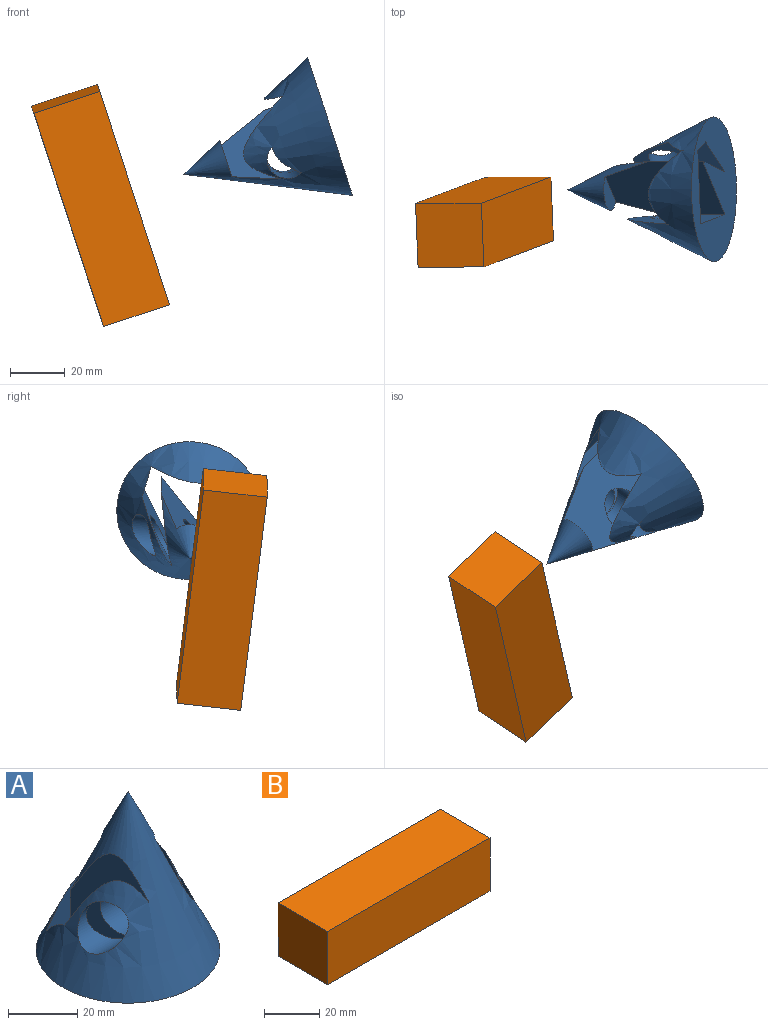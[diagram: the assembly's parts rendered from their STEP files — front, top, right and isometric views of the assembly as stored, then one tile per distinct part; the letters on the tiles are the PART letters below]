
ASSEMBLY  parts=2 mates=1
PART A: 12 faces, bbox 55.3x55.3x58.5 mm
  f0: plane 53.16x53.16mm, normal (0,0,-1), area 1696.5mm2, adj f2,f6,f7,f8,f9,f10,f11
  f1: cylinder r=7.21mm len=25.05mm, axis (-1,0,0), area 694mm2, adj f2,f4,f8,f9,f10
  f2: cone r=26.58mm half-angle=25.2deg, axis (0,0,-1), area 3909.5mm2, adj f0,f1,f3,f4,f5,f6,f7,f8
  f3: cylinder r=7.21mm len=15.14mm, axis (-1,0,0), area 265.4mm2, adj f2,f11
  f4: plane 13.37x10.95mm, normal (-1,0,0), area 98.6mm2, adj f1,f2
  f5: plane 13.47x13.25mm, normal (0,0,-1), area 97.6mm2, adj f2,f9
  f6: plane 26.97x19.73mm, normal (0,-1,0), area 429.8mm2, adj f0,f2,f7,f8
  f7: plane 16.27x11.73mm, normal (0.97,-0.22,0), area 106.1mm2, adj f0,f2,f6,f11
  f8: plane 33.5x28.91mm, normal (-1,0,0), area 630.2mm2, adj f0,f1,f2,f6,f9
  f9: plane 41.38x24.9mm, normal (0.72,0.69,0), area 923.7mm2, adj f0,f1,f2,f5,f8,f10
  f10: plane 39.04x25.37mm, normal (-0.96,-0.26,0), area 693.9mm2, adj f0,f1,f2,f9,f11
  f11: plane 34.14x22.86mm, normal (0.84,0.54,0), area 485.6mm2, adj f0,f2,f3,f7,f10
PART B: 6 faces, bbox 82.8x25.4x23.5 mm
  f0: plane 82.83x25.4mm, normal (0,0,1), area 2103.8mm2, adj f1,f3,f4,f5
  f1: plane 25.4x23.53mm, normal (-1,0,0), area 597.5mm2, adj f0,f2,f4,f5
  f2: plane 82.83x25.4mm, normal (0,0,-1), area 2103.8mm2, adj f1,f3,f4,f5
  f3: plane 25.4x23.53mm, normal (1,0,0), area 597.5mm2, adj f0,f2,f4,f5
  f4: plane 82.83x23.53mm, normal (0,-1,0), area 1948.5mm2, adj f0,f1,f2,f3
  f5: plane 82.83x23.53mm, normal (0,1,0), area 1948.5mm2, adj f0,f1,f2,f3
PLACE A rot(axis=(0.66,-0.58,-0.48),133.9deg) t=(110.51,-55.13,38.07)mm
PLACE B rot(axis=(0.49,-0.64,0.59),135.3deg) t=(16.3,-114.43,-19.87)mm fixed
MATE slider A.f2 <-> B.f4  axis (-0.95,0,-0.31) through (51.55,-63.53,17.8)mm
